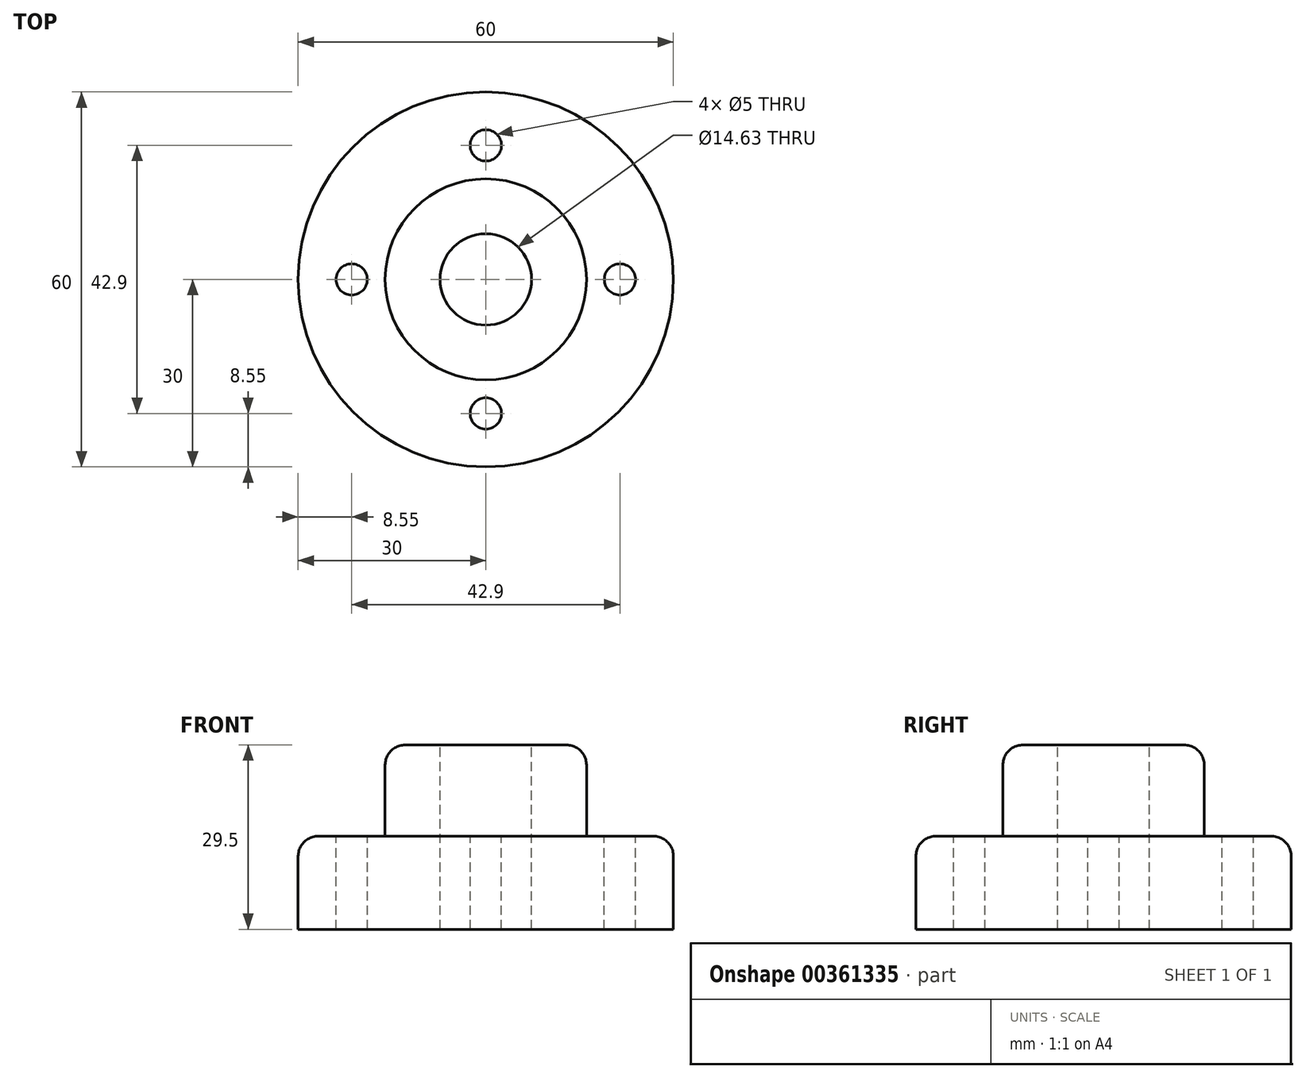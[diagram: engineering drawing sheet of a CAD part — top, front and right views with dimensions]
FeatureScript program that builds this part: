
annotation { "Feature Type Name" : "Feature", "Feature Type Description" : "" }
export const myFeature = defineFeature(function(context is Context, id is Id, definition is map)
    precondition{}
    {
        {
            var Q0;
            Q0=qCreatedBy(makeId("Top.planeOp"),FACE);
            var sketch = newSketch(context, id + "F0", { "sketchPlane" : qUnion([Q0])});
            skCircle(sketch, "E0", {"center": v(0, 0) * mm, "radius": 30 * mm});
            skCircle(sketch, "E1", {"center": v(0, 0) * mm, "radius": 16.1 * mm});
            skSolve(sketch);
        }
        {
            var Q0;
            Q0=makeQuery(id+"F0.imprint","IMPRINT",FACE,{"disambiguationData":[TD([[makeQuery(id+"F0.imprint","IMPRINT",EDGE,{"derivedFrom":sQuery(id+"F0.wireOp",EDGE,"E0")}),1.0]])]});
            extrude(context, id + "F1", {"entities" : qUnion([Q0]), "depth" : 14.9 * mm});
        }
        {
            var Q0;
            Q0=makeQuery(id+"F0.imprint","IMPRINT",FACE,{"disambiguationData":[TD([[makeQuery(id+"F0.imprint","IMPRINT",EDGE,{"derivedFrom":sQuery(id+"F0.wireOp",EDGE,"E1")}),1.0]])]});
            extrude(context, id + "F2", {"entities" : qUnion([Q0]), "operationType" : NewBodyOperationType.ADD, "depth" : 29.5 * mm});
        }
        {
            var Q0;
            Q0=makeQuery(id+"F1.opExtrude","CAP_EDGE",EDGE,{"disambiguationData":[OSD([sQuery(id+"F0.wireOp",EDGE,"E0")])],"isStart":false});
            fillet(context, id + "F3", {"entities" : qUnion([Q0]), "radius" : 3.2 * mm, "tangentPropagation" : true, "allowEdgeOverflow" : false});
        }
        {
            var Q0;
            Q0=makeQuery(id+"F2.opExtrude","CAP_EDGE",EDGE,{"disambiguationData":[OSD([sQuery(id+"F0.wireOp",EDGE,"E1")])],"isStart":false});
            fillet(context, id + "F4", {"entities" : qUnion([Q0]), "radius" : 3.2 * mm, "tangentPropagation" : true, "allowEdgeOverflow" : false});
        }
        {
            var Q0;
            Q0=makeQuery(id+"F1.opExtrude","CAP_FACE",FACE,{"disambiguationData":[OSD([sQuery(id+"F0.wireOp",EDGE,"E0"),sQuery(id+"F0.wireOp",EDGE,"E1")])],"isStart":false});
            var sketch = newSketch(context, id + "F5", { "sketchPlane" : qUnion([Q0])});
            skCircle(sketch, "E2", {"center": v(0, 21.45) * mm, "radius": 2.5 * mm});
            skLineSegment(sketch, "E3", {"start": v(16.1, 0) * mm, "end": v(18.95, 0) * mm});
            skLineSegment(sketch, "E4", {"start": v(0, -16.1) * mm, "end": v(0, -18.95) * mm});
            skCircle(sketch, "E5", {"center": v(-21.45, 0) * mm, "radius": 2.5 * mm});
            skCircle(sketch, "E6", {"center": v(21.45, 0) * mm, "radius": 2.5 * mm});
            skCircle(sketch, "E7", {"center": v(0, -21.45) * mm, "radius": 2.5 * mm});
            skPoint(sketch, "E8.orphan", {"position": v(-16.1, 0) * mm});
            skPoint(sketch, "E9.trimOffspring.end.orphan", {"position": v(-26.8, 0) * mm});
            skPoint(sketch, "E10.orphan", {"position": v(0, 26.8) * mm});
            skPoint(sketch, "E11.start.orphan", {"position": v(0, 16.1) * mm});
            skPoint(sketch, "E12.trimOffspring.end.orphan", {"position": v(26.8, 0) * mm});
            skLineSegment(sketch, "E13.trimOffspring", {"start": v(0, -23.95) * mm, "end": v(0, -26.8) * mm});
            skSolve(sketch);
        }
        {
            var Q0;
            Q0=makeQuery(id+"F5.imprint","IMPRINT",FACE,{"disambiguationData":[TD([[makeQuery(id+"F5.imprint","IMPRINT",EDGE,{"derivedFrom":sQuery(id+"F5.wireOp",EDGE,"E5")}),1.0]])]});
            var Q1;
            Q1=makeQuery(id+"F5.imprint","IMPRINT",FACE,{"disambiguationData":[TD([[makeQuery(id+"F5.imprint","IMPRINT",EDGE,{"derivedFrom":sQuery(id+"F5.wireOp",EDGE,"E2")}),1.0]])]});
            var Q2;
            Q2=makeQuery(id+"F5.imprint","IMPRINT",FACE,{"disambiguationData":[TD([[makeQuery(id+"F5.imprint","IMPRINT",EDGE,{"derivedFrom":sQuery(id+"F5.wireOp",EDGE,"E6")}),1.0]])]});
            var Q3;
            {var subQ0=sQuery(id+"F5.wireOp",EDGE,"E7");var subQ1=makeQuery(id+"F5.imprint","IMPRINT",VERTEX,{"disambiguationData":[OD(0.0)],"derivedFrom":subQ0});Q3=makeQuery(id+"F5.imprint","IMPRINT",FACE,{"disambiguationData":[TD([[makeQuery(id+"F5.imprint","IMPRINT",EDGE,{"disambiguationData":[TD([[subQ1,-1.0]])],"derivedFrom":subQ0}),1.0]])]});}
            extrude(context, id + "F6", {"entities" : qUnion([Q0, Q1, Q2, Q3]), "operationType" : NewBodyOperationType.REMOVE, "oppositeDirection" : true, "depth" : 100 * mm});
        }
        {
            var Q0;
            Q0=makeQuery(id+"F2.opExtrude","CAP_FACE",FACE,{"disambiguationData":[OSD([sQuery(id+"F0.wireOp",EDGE,"E1")])],"isStart":false});
            var sketch = newSketch(context, id + "F7", { "sketchPlane" : qUnion([Q0])});
            skCircle(sketch, "E14", {"center": v(0, 0) * mm, "radius": 7.32 * mm});
            skSolve(sketch);
        }
        {
            var Q0;
            Q0=makeQuery(id+"F7.imprint","IMPRINT",FACE,{"disambiguationData":[TD([[makeQuery(id+"F7.imprint","IMPRINT",EDGE,{"derivedFrom":sQuery(id+"F7.wireOp",EDGE,"E14")}),1.0]])]});
            extrude(context, id + "F8", {"entities" : qUnion([Q0]), "operationType" : NewBodyOperationType.REMOVE, "oppositeDirection" : true, "depth" : 100 * mm});
        }
    });
